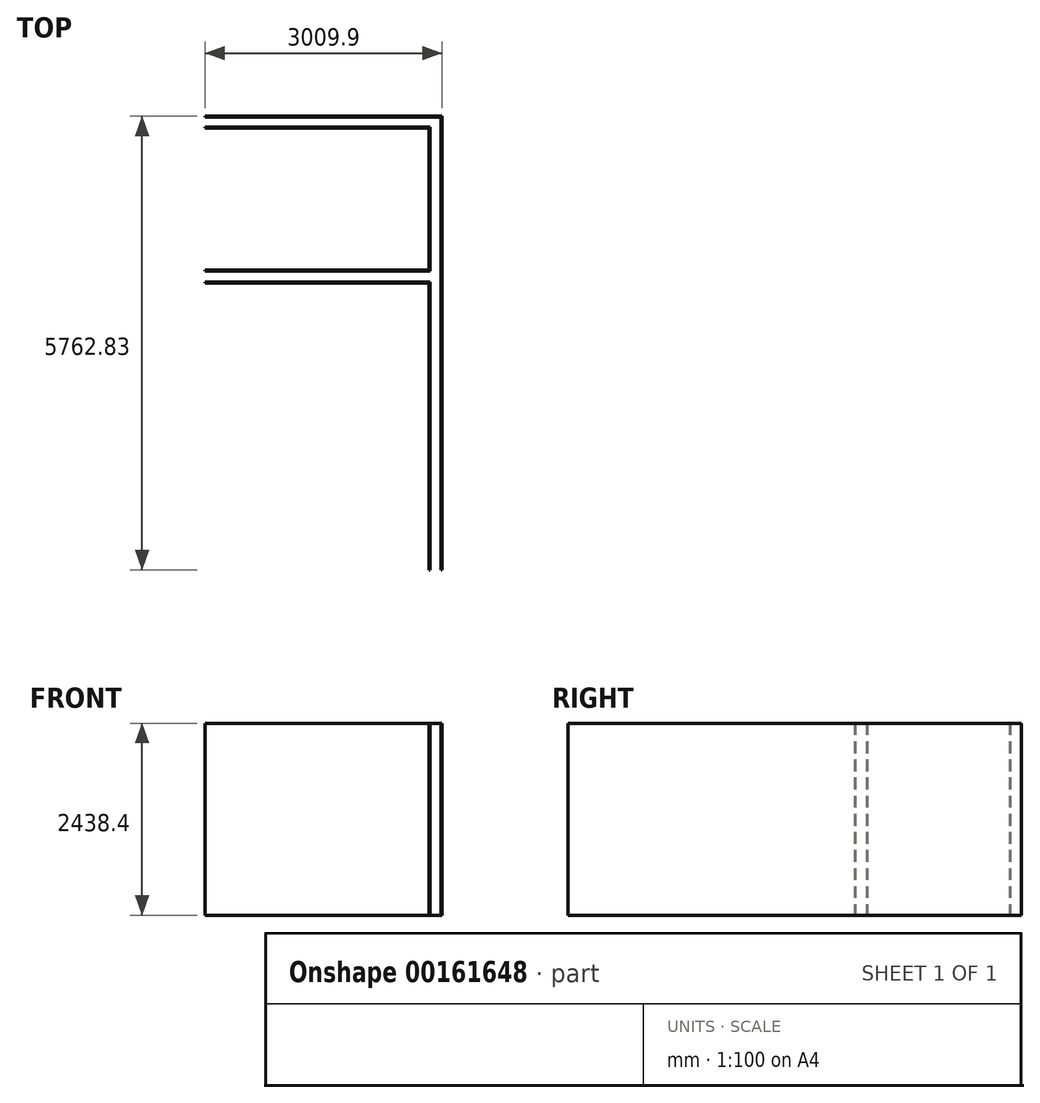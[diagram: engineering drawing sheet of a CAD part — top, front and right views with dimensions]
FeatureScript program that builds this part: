
annotation { "Feature Type Name" : "Feature", "Feature Type Description" : "" }
export const myFeature = defineFeature(function(context is Context, id is Id, definition is map)
    precondition{}
    {
        {
            var Q0;
            Q0=qCreatedBy(makeId("Top.planeOp"),FACE);
            var sketch = newSketch(context, id + "F0", { "sketchPlane" : qUnion([Q0])});
            skLineSegment(sketch, "E0", {"start": v(-8280.4, 16078.2) * mm, "end": v(-2286, 16078.2) * mm});
            skLineSegment(sketch, "E1", {"start": v(-2286, 16078.2) * mm, "end": v(-2286, 7162.8) * mm});
            skLineSegment(sketch, "E2", {"start": v(-2286, 7162.8) * mm, "end": v(0, 7162.8) * mm});
            skLineSegment(sketch, "E3", {"start": v(0, 7162.8) * mm, "end": v(0, 0) * mm});
            skLineSegment(sketch, "E4", {"start": v(0, 0) * mm, "end": v(-5283.2, 0) * mm});
            skLineSegment(sketch, "E5", {"start": v(-5283.2, 0) * mm, "end": v(-5283.2, 2286) * mm});
            skLineSegment(sketch, "E6", {"start": v(-5283.2, 2286) * mm, "end": v(-8280.4, 2286) * mm});
            skLineSegment(sketch, "E7", {"start": v(-8280.4, 2286) * mm, "end": v(-8280.4, 8201.03) * mm});
            skLineSegment(sketch, "E8", {"start": v(-8280.4, 8201.03) * mm, "end": v(-9406.5, 8900.32) * mm});
            skLineSegment(sketch, "E9", {"start": v(-9406.5, 8900.32) * mm, "end": v(-9406.5, 13223.08) * mm});
            skLineSegment(sketch, "E10", {"start": v(-9406.5, 13223.08) * mm, "end": v(-8280.4, 13922.38) * mm});
            skLineSegment(sketch, "E11", {"start": v(-8280.4, 13922.38) * mm, "end": v(-8280.4, 16078.2) * mm});
            skSolve(sketch);
        }
        {
            var Q0;
            Q0=qSketchRegion(id+"F0",true);
            extrude(context, id + "F1", {"entities" : qUnion([Q0]), "depth" : 2578.1 * mm});
        }
        {
            var Q0;
            Q0=makeQuery(id+"F1.opExtrude","CAP_FACE",FACE,{"disambiguationData":[OSD([sQuery(id+"F0.wireOp",EDGE,"E0"),sQuery(id+"F0.wireOp",EDGE,"E1"),sQuery(id+"F0.wireOp",EDGE,"E2"),sQuery(id+"F0.wireOp",EDGE,"E3"),sQuery(id+"F0.wireOp",EDGE,"E4"),sQuery(id+"F0.wireOp",EDGE,"E5"),sQuery(id+"F0.wireOp",EDGE,"E6"),sQuery(id+"F0.wireOp",EDGE,"E7"),sQuery(id+"F0.wireOp",EDGE,"E8"),sQuery(id+"F0.wireOp",EDGE,"E9"),sQuery(id+"F0.wireOp",EDGE,"E10"),sQuery(id+"F0.wireOp",EDGE,"E11")])],"isStart":false});
            shell(context, id + "F2", {"entities" : qUnion([Q0]), "thickness" : 203.2 * mm});
        }
        {
            var Q0;
            Q0=makeQuery(id+"F2.opShell","OFFSET_FACE",FACE,{"disambiguationData":[OSD([sQuery(id+"F0.wireOp",EDGE,"E6")])]});
            var sketch = newSketch(context, id + "F3", { "sketchPlane" : qUnion([Q0])});
            skLineSegment(sketch, "E12.bottom", {"start": v(5969, 2324.1) * mm, "end": v(7188.2, 2324.1) * mm});
            skLineSegment(sketch, "E12.top", {"start": v(5969, 901.7) * mm, "end": v(7188.2, 901.7) * mm});
            skLineSegment(sketch, "E12.left", {"start": v(5969, 2324.1) * mm, "end": v(5969, 901.7) * mm});
            skLineSegment(sketch, "E12.right", {"start": v(7188.2, 2324.1) * mm, "end": v(7188.2, 901.7) * mm});
            skPoint(sketch, "E13", {"position": v(6578.6, 2324.1) * mm});
            skSolve(sketch);
        }
        {
            var Q0;
            Q0=makeQuery(id+"F2.opShell","OFFSET_FACE",FACE,{"disambiguationData":[OSD([sQuery(id+"F0.wireOp",EDGE,"E0"),sQuery(id+"F0.wireOp",EDGE,"E1"),sQuery(id+"F0.wireOp",EDGE,"E2"),sQuery(id+"F0.wireOp",EDGE,"E3"),sQuery(id+"F0.wireOp",EDGE,"E4"),sQuery(id+"F0.wireOp",EDGE,"E5"),sQuery(id+"F0.wireOp",EDGE,"E6"),sQuery(id+"F0.wireOp",EDGE,"E7"),sQuery(id+"F0.wireOp",EDGE,"E8"),sQuery(id+"F0.wireOp",EDGE,"E9"),sQuery(id+"F0.wireOp",EDGE,"E10"),sQuery(id+"F0.wireOp",EDGE,"E11")])]});
            var sketch = newSketch(context, id + "F4", { "sketchPlane" : qUnion([Q0])});
            skLineSegment(sketch, "E14.bottom", {"start": v(-8077.2, 13811.9) * mm, "end": v(-7937.5, 13811.9) * mm});
            skLineSegment(sketch, "E14.top", {"start": v(-8077.2, 13850) * mm, "end": v(-7937.5, 13850) * mm});
            skLineSegment(sketch, "E14.left", {"start": v(-8077.2, 13811.9) * mm, "end": v(-8077.2, 13850) * mm});
            skLineSegment(sketch, "E14.right", {"start": v(-7937.5, 13811.9) * mm, "end": v(-7937.5, 13850) * mm});
            skLineSegment(sketch, "E15.bottom", {"start": v(-7934.96, 15875) * mm, "end": v(-7896.86, 15875) * mm});
            skLineSegment(sketch, "E15.top", {"start": v(-7934.96, 15735.3) * mm, "end": v(-7896.86, 15735.3) * mm});
            skLineSegment(sketch, "E15.left", {"start": v(-7934.96, 15875) * mm, "end": v(-7934.96, 15735.3) * mm});
            skLineSegment(sketch, "E15.right", {"start": v(-7896.86, 15875) * mm, "end": v(-7896.86, 15735.3) * mm});
            skLineSegment(sketch, "E16.bottom", {"start": v(-8077.2, 15694.66) * mm, "end": v(-7937.5, 15694.66) * mm});
            skLineSegment(sketch, "E16.top", {"start": v(-8077.2, 15732.76) * mm, "end": v(-7937.5, 15732.76) * mm});
            skLineSegment(sketch, "E16.left", {"start": v(-8077.2, 15694.66) * mm, "end": v(-8077.2, 15732.76) * mm});
            skLineSegment(sketch, "E16.right", {"start": v(-7937.5, 15694.66) * mm, "end": v(-7937.5, 15732.76) * mm});
            skLineSegment(sketch, "E17.bottom", {"start": v(-2631.44, 15875) * mm, "end": v(-2669.54, 15875) * mm});
            skLineSegment(sketch, "E17.top", {"start": v(-2631.44, 15735.3) * mm, "end": v(-2669.54, 15735.3) * mm});
            skLineSegment(sketch, "E17.left", {"start": v(-2631.44, 15875) * mm, "end": v(-2631.44, 15735.3) * mm});
            skLineSegment(sketch, "E17.right", {"start": v(-2669.54, 15875) * mm, "end": v(-2669.54, 15735.3) * mm});
            skLineSegment(sketch, "E18.bottom", {"start": v(-2489.2, 15694.66) * mm, "end": v(-2628.9, 15694.66) * mm});
            skLineSegment(sketch, "E18.top", {"start": v(-2489.2, 15732.76) * mm, "end": v(-2628.9, 15732.76) * mm});
            skLineSegment(sketch, "E18.left", {"start": v(-2489.2, 15694.66) * mm, "end": v(-2489.2, 15732.76) * mm});
            skLineSegment(sketch, "E18.right", {"start": v(-2628.9, 15694.66) * mm, "end": v(-2628.9, 15732.76) * mm});
            skLineSegment(sketch, "E19", {"start": v(-8078.22, 13808.73) * mm, "end": v(-8110.59, 13788.64) * mm});
            skLineSegment(sketch, "E20", {"start": v(-8110.59, 13788.64) * mm, "end": v(-8036.89, 13669.96) * mm});
            skLineSegment(sketch, "E21", {"start": v(-8036.89, 13669.96) * mm, "end": v(-8004.52, 13690.06) * mm});
            skLineSegment(sketch, "E22", {"start": v(-8004.52, 13690.06) * mm, "end": v(-8078.22, 13808.73) * mm});
            skLineSegment(sketch, "E23.bottom", {"start": v(-9203.3, 12669.47) * mm, "end": v(-9063.6, 12669.47) * mm});
            skLineSegment(sketch, "E23.top", {"start": v(-9203.3, 12631.37) * mm, "end": v(-9063.6, 12631.37) * mm});
            skLineSegment(sketch, "E23.left", {"start": v(-9203.3, 12669.47) * mm, "end": v(-9203.3, 12631.37) * mm});
            skLineSegment(sketch, "E23.right", {"start": v(-9063.6, 12669.47) * mm, "end": v(-9063.6, 12631.37) * mm});
            skLineSegment(sketch, "E24", {"start": v(-9162.3, 13135.53) * mm, "end": v(-9129.94, 13155.63) * mm});
            skLineSegment(sketch, "E25", {"start": v(-9129.94, 13155.63) * mm, "end": v(-9056.24, 13036.95) * mm});
            skLineSegment(sketch, "E26", {"start": v(-9056.24, 13036.95) * mm, "end": v(-9088.6, 13016.85) * mm});
            skLineSegment(sketch, "E27", {"start": v(-9088.6, 13016.85) * mm, "end": v(-9162.3, 13135.53) * mm});
            skLineSegment(sketch, "E28", {"start": v(-9162.3, 8987.87) * mm, "end": v(-9088.6, 9106.55) * mm});
            skLineSegment(sketch, "E29", {"start": v(-9088.6, 9106.55) * mm, "end": v(-9056.24, 9086.45) * mm});
            skLineSegment(sketch, "E30", {"start": v(-9056.24, 9086.45) * mm, "end": v(-9129.94, 8967.77) * mm});
            skLineSegment(sketch, "E31", {"start": v(-9129.94, 8967.77) * mm, "end": v(-9162.3, 8987.87) * mm});
            skLineSegment(sketch, "E32", {"start": v(-8109.57, 8334.13) * mm, "end": v(-8077.2, 8314.03) * mm});
            skLineSegment(sketch, "E33", {"start": v(-8077.2, 8314.03) * mm, "end": v(-8003.5, 8432.71) * mm});
            skLineSegment(sketch, "E34", {"start": v(-8003.5, 8432.71) * mm, "end": v(-8035.87, 8452.81) * mm});
            skLineSegment(sketch, "E35", {"start": v(-8035.87, 8452.81) * mm, "end": v(-8109.57, 8334.13) * mm});
            skLineSegment(sketch, "E36.bottom", {"start": v(-9203.3, 9061.59) * mm, "end": v(-9063.6, 9061.59) * mm});
            skLineSegment(sketch, "E36.top", {"start": v(-9203.3, 9099.69) * mm, "end": v(-9063.6, 9099.69) * mm});
            skLineSegment(sketch, "E36.left", {"start": v(-9203.3, 9061.59) * mm, "end": v(-9203.3, 9099.69) * mm});
            skLineSegment(sketch, "E36.right", {"start": v(-9063.6, 9061.59) * mm, "end": v(-9063.6, 9099.69) * mm});
            skLineSegment(sketch, "E37.bottom", {"start": v(-8077.2, 8311.5) * mm, "end": v(-7937.5, 8311.5) * mm});
            skLineSegment(sketch, "E37.top", {"start": v(-8077.2, 8273.4) * mm, "end": v(-7937.5, 8273.4) * mm});
            skLineSegment(sketch, "E37.left", {"start": v(-8077.2, 8311.5) * mm, "end": v(-8077.2, 8273.4) * mm});
            skLineSegment(sketch, "E37.right", {"start": v(-7937.5, 8311.5) * mm, "end": v(-7937.5, 8273.4) * mm});
            skLineSegment(sketch, "E38.bottom", {"start": v(-8077.2, 2631.44) * mm, "end": v(-7937.5, 2631.44) * mm});
            skLineSegment(sketch, "E38.top", {"start": v(-8077.2, 2669.54) * mm, "end": v(-7937.5, 2669.54) * mm});
            skLineSegment(sketch, "E38.left", {"start": v(-8077.2, 2631.44) * mm, "end": v(-8077.2, 2669.54) * mm});
            skLineSegment(sketch, "E38.right", {"start": v(-7937.5, 2631.44) * mm, "end": v(-7937.5, 2669.54) * mm});
            skLineSegment(sketch, "E39.bottom", {"start": v(-7896.86, 2489.2) * mm, "end": v(-7934.96, 2489.2) * mm});
            skLineSegment(sketch, "E39.top", {"start": v(-7896.86, 2628.9) * mm, "end": v(-7934.96, 2628.9) * mm});
            skLineSegment(sketch, "E39.left", {"start": v(-7896.86, 2489.2) * mm, "end": v(-7896.86, 2628.9) * mm});
            skLineSegment(sketch, "E39.right", {"start": v(-7934.96, 2489.2) * mm, "end": v(-7934.96, 2628.9) * mm});
            skLineSegment(sketch, "E40.bottom", {"start": v(-5082.54, 2489.2) * mm, "end": v(-5120.64, 2489.2) * mm});
            skLineSegment(sketch, "E40.top", {"start": v(-5082.54, 2628.9) * mm, "end": v(-5120.64, 2628.9) * mm});
            skLineSegment(sketch, "E40.left", {"start": v(-5082.54, 2489.2) * mm, "end": v(-5082.54, 2628.9) * mm});
            skLineSegment(sketch, "E40.right", {"start": v(-5120.64, 2489.2) * mm, "end": v(-5120.64, 2628.9) * mm});
            skLineSegment(sketch, "E41.top", {"start": v(-5080, 2448.56) * mm, "end": v(-4940.3, 2448.56) * mm});
            skLineSegment(sketch, "E41.right", {"start": v(-4940.3, 2486.66) * mm, "end": v(-4940.3, 2448.56) * mm});
            skLineSegment(sketch, "E42.bottom", {"start": v(-5080, 345.44) * mm, "end": v(-4940.3, 345.44) * mm});
            skLineSegment(sketch, "E42.top", {"start": v(-5080, 383.54) * mm, "end": v(-4940.3, 383.54) * mm});
            skLineSegment(sketch, "E42.left", {"start": v(-5080, 345.44) * mm, "end": v(-5080, 383.54) * mm});
            skLineSegment(sketch, "E42.right", {"start": v(-4940.3, 345.44) * mm, "end": v(-4940.3, 383.54) * mm});
            skLineSegment(sketch, "E43.bottom", {"start": v(-4937.76, 203.2) * mm, "end": v(-4899.66, 203.2) * mm});
            skLineSegment(sketch, "E43.top", {"start": v(-4937.76, 342.9) * mm, "end": v(-4899.66, 342.9) * mm});
            skLineSegment(sketch, "E43.left", {"start": v(-4937.76, 203.2) * mm, "end": v(-4937.76, 342.9) * mm});
            skLineSegment(sketch, "E43.right", {"start": v(-4899.66, 203.2) * mm, "end": v(-4899.66, 342.9) * mm});
            skLineSegment(sketch, "E44.bottom", {"start": v(-383.54, 203.2) * mm, "end": v(-345.44, 203.2) * mm});
            skLineSegment(sketch, "E44.top", {"start": v(-383.54, 342.9) * mm, "end": v(-345.44, 342.9) * mm});
            skLineSegment(sketch, "E44.left", {"start": v(-383.54, 203.2) * mm, "end": v(-383.54, 342.9) * mm});
            skLineSegment(sketch, "E44.right", {"start": v(-345.44, 203.2) * mm, "end": v(-345.44, 342.9) * mm});
            skLineSegment(sketch, "E45.bottom", {"start": v(-203.2, 345.44) * mm, "end": v(-342.9, 345.44) * mm});
            skLineSegment(sketch, "E45.top", {"start": v(-203.2, 383.54) * mm, "end": v(-342.9, 383.54) * mm});
            skLineSegment(sketch, "E45.left", {"start": v(-203.2, 345.44) * mm, "end": v(-203.2, 383.54) * mm});
            skLineSegment(sketch, "E45.right", {"start": v(-342.9, 345.44) * mm, "end": v(-342.9, 383.54) * mm});
            skLineSegment(sketch, "E46.bottom", {"start": v(-203.2, 6779.26) * mm, "end": v(-342.9, 6779.26) * mm});
            skLineSegment(sketch, "E46.top", {"start": v(-203.2, 6817.36) * mm, "end": v(-342.9, 6817.36) * mm});
            skLineSegment(sketch, "E46.left", {"start": v(-203.2, 6779.26) * mm, "end": v(-203.2, 6817.36) * mm});
            skLineSegment(sketch, "E46.right", {"start": v(-342.9, 6779.26) * mm, "end": v(-342.9, 6817.36) * mm});
            skLineSegment(sketch, "E47.bottom", {"start": v(-345.44, 6959.6) * mm, "end": v(-383.54, 6959.6) * mm});
            skLineSegment(sketch, "E47.top", {"start": v(-345.44, 6819.9) * mm, "end": v(-383.54, 6819.9) * mm});
            skLineSegment(sketch, "E47.left", {"start": v(-345.44, 6959.6) * mm, "end": v(-345.44, 6819.9) * mm});
            skLineSegment(sketch, "E47.right", {"start": v(-383.54, 6959.6) * mm, "end": v(-383.54, 6819.9) * mm});
            skLineSegment(sketch, "E48", {"start": v(-4940.3, 2486.66) * mm, "end": v(-5080, 2486.66) * mm});
            skLineSegment(sketch, "E49", {"start": v(-5080, 2486.66) * mm, "end": v(-5080, 2448.56) * mm});
            skLineSegment(sketch, "E50", {"start": v(-9203.3, 13110.07) * mm, "end": v(-9045.7, 12987.43) * mm, "construction": true});
            skLineSegment(sketch, "E51", {"start": v(-9045.7, 12987.43) * mm, "end": v(-9104.83, 13171.22) * mm, "construction": true});
            skLineSegment(sketch, "E52", {"start": v(-9104.83, 13171.22) * mm, "end": v(-9203.3, 12968.55) * mm, "construction": true});
            skLineSegment(sketch, "E53", {"start": v(-9203.3, 12968.55) * mm, "end": v(-9045.7, 12987.43) * mm, "construction": true});
            skSolve(sketch);
        }
        {
            var Q0;
            Q0=qSketchRegion(id+"F3",true);
            var Q1;
            Q1=makeQuery(id+"FwcOo8eikqoZCvb_1.opExtrude","SWEPT_FACE",FACE,{"disambiguationData":[OSD([sQuery(id+"F7.wireOp",EDGE,"E55.top"),sQuery(id+"F7.wireOp",EDGE,"E63")])]});
            extrude(context, id + "F5", {"entities" : qUnion([Q0]), "operationType" : NewBodyOperationType.REMOVE, "endBound" : BoundingType.UP_TO_NEXT, "oppositeDirection" : true, "depth" : 25.4 * mm});
        }
        {
            var Q0;
            Q0=qSketchRegion(id+"F4",true);
            extrude(context, id + "F6", {"entities" : qUnion([Q0]), "operationType" : NewBodyOperationType.ADD, "depth" : 2349.5 * mm});
        }
        {
            var Q0;
            Q0=makeQuery(id+"F2.opShell","OFFSET_FACE",FACE,{"disambiguationData":[OSD([sQuery(id+"F0.wireOp",EDGE,"E0"),sQuery(id+"F0.wireOp",EDGE,"E1"),sQuery(id+"F0.wireOp",EDGE,"E2"),sQuery(id+"F0.wireOp",EDGE,"E3"),sQuery(id+"F0.wireOp",EDGE,"E4"),sQuery(id+"F0.wireOp",EDGE,"E5"),sQuery(id+"F0.wireOp",EDGE,"E6"),sQuery(id+"F0.wireOp",EDGE,"E7"),sQuery(id+"F0.wireOp",EDGE,"E8"),sQuery(id+"F0.wireOp",EDGE,"E9"),sQuery(id+"F0.wireOp",EDGE,"E10"),sQuery(id+"F0.wireOp",EDGE,"E11")])]});
            var sketch = newSketch(context, id + "F7", { "sketchPlane" : qUnion([Q0])});
            skLineSegment(sketch, "E54.bottom", {"start": v(-7937.5, 8391.73) * mm, "end": v(-7924.8, 8391.73) * mm, "construction": true});
            skLineSegment(sketch, "E54.top", {"start": v(-7937.5, 2641.6) * mm, "end": v(-7924.8, 2641.6) * mm, "construction": true});
            skLineSegment(sketch, "E54.left", {"start": v(-7937.5, 8391.73) * mm, "end": v(-7937.5, 2641.6) * mm});
            skLineSegment(sketch, "E54.right", {"start": v(-7924.8, 8391.73) * mm, "end": v(-7924.8, 2641.6) * mm});
            skLineSegment(sketch, "E55.bottom", {"start": v(-7924.8, 2628.9) * mm, "end": v(-4940.3, 2628.9) * mm});
            skLineSegment(sketch, "E55.top", {"start": v(-7924.8, 2641.6) * mm, "end": v(-4940.3, 2641.6) * mm});
            skLineSegment(sketch, "E55.left", {"start": v(-7924.8, 2628.9) * mm, "end": v(-7924.8, 2641.6) * mm, "construction": true});
            skLineSegment(sketch, "E55.right", {"start": v(-4940.3, 2628.9) * mm, "end": v(-4940.3, 2641.6) * mm, "construction": true});
            skLineSegment(sketch, "E56", {"start": v(-7924.8, 2628.9) * mm, "end": v(-7937.5, 2628.9) * mm});
            skLineSegment(sketch, "E57", {"start": v(-7937.5, 2628.9) * mm, "end": v(-7937.5, 2641.6) * mm});
            skLineSegment(sketch, "E58.bottom", {"start": v(-4940.3, 2628.9) * mm, "end": v(-4927.6, 2628.9) * mm, "construction": true});
            skLineSegment(sketch, "E58.top", {"start": v(-4940.3, 355.6) * mm, "end": v(-4927.6, 355.6) * mm, "construction": true});
            skLineSegment(sketch, "E58.left", {"start": v(-4940.3, 2628.9) * mm, "end": v(-4940.3, 355.6) * mm});
            skLineSegment(sketch, "E58.right", {"start": v(-4927.6, 2628.9) * mm, "end": v(-4927.6, 355.6) * mm});
            skLineSegment(sketch, "E59.bottom", {"start": v(-4927.6, 342.9) * mm, "end": v(-355.6, 342.9) * mm});
            skLineSegment(sketch, "E59.top", {"start": v(-4927.6, 355.6) * mm, "end": v(-355.6, 355.6) * mm});
            skLineSegment(sketch, "E59.left", {"start": v(-4927.6, 342.9) * mm, "end": v(-4927.6, 355.6) * mm, "construction": true});
            skLineSegment(sketch, "E59.right", {"start": v(-355.6, 342.9) * mm, "end": v(-355.6, 355.6) * mm, "construction": true});
            skLineSegment(sketch, "E60", {"start": v(-4940.3, 355.6) * mm, "end": v(-4940.3, 342.9) * mm});
            skLineSegment(sketch, "E61", {"start": v(-4940.3, 342.9) * mm, "end": v(-4927.6, 342.9) * mm});
            skLineSegment(sketch, "E62", {"start": v(-4927.6, 2628.9) * mm, "end": v(-4927.6, 2641.6) * mm});
            skLineSegment(sketch, "E63", {"start": v(-4940.3, 2641.6) * mm, "end": v(-4927.6, 2641.6) * mm});
            skLineSegment(sketch, "E64.bottom", {"start": v(-355.6, 355.6) * mm, "end": v(-342.9, 355.6) * mm, "construction": true});
            skLineSegment(sketch, "E64.top", {"start": v(-355.6, 6019.58) * mm, "end": v(-342.9, 6019.58) * mm});
            skLineSegment(sketch, "E64.left", {"start": v(-355.6, 355.6) * mm, "end": v(-355.6, 6019.58) * mm});
            skLineSegment(sketch, "E64.right", {"start": v(-342.9, 355.6) * mm, "end": v(-342.9, 6019.58) * mm});
            skLineSegment(sketch, "E65", {"start": v(-355.6, 342.9) * mm, "end": v(-342.9, 342.9) * mm});
            skLineSegment(sketch, "E66", {"start": v(-342.9, 342.9) * mm, "end": v(-342.9, 355.6) * mm});
            skLineSegment(sketch, "E67", {"start": v(-7937.5, 8391.73) * mm, "end": v(-9063.6, 9091.02) * mm});
            skLineSegment(sketch, "E68", {"start": v(-9063.6, 9091.02) * mm, "end": v(-9063.6, 13032.38) * mm});
            skLineSegment(sketch, "E69", {"start": v(-9063.6, 13032.38) * mm, "end": v(-7937.5, 13731.67) * mm});
            skLineSegment(sketch, "E70", {"start": v(-7937.5, 13731.67) * mm, "end": v(-7937.5, 15735.3) * mm});
            skLineSegment(sketch, "E71", {"start": v(-7937.5, 15735.3) * mm, "end": v(-2628.9, 15735.3) * mm});
            skLineSegment(sketch, "E72", {"start": v(-2628.9, 15735.3) * mm, "end": v(-2628.9, 11339.58) * mm});
            skLineSegment(sketch, "E73", {"start": v(-2628.9, 11339.58) * mm, "end": v(-2641.6, 11339.58) * mm});
            skLineSegment(sketch, "E74", {"start": v(-2641.6, 11339.58) * mm, "end": v(-2641.6, 15722.6) * mm});
            skLineSegment(sketch, "E75", {"start": v(-2641.6, 15722.6) * mm, "end": v(-7924.8, 15722.6) * mm});
            skLineSegment(sketch, "E76", {"start": v(-7924.8, 15722.6) * mm, "end": v(-7924.8, 13724.61) * mm});
            skLineSegment(sketch, "E77", {"start": v(-7924.8, 13724.61) * mm, "end": v(-9050.9, 13025.32) * mm});
            skLineSegment(sketch, "E78", {"start": v(-9050.9, 13025.32) * mm, "end": v(-9050.9, 9098.08) * mm});
            skLineSegment(sketch, "E79", {"start": v(-9050.9, 9098.08) * mm, "end": v(-7924.8, 8398.79) * mm});
            skLineSegment(sketch, "E80", {"start": v(-8493.85, 8752.16) * mm, "end": v(-8500.55, 8741.37) * mm, "construction": true});
            skLineSegment(sketch, "E81", {"start": v(-9063.6, 11061.7) * mm, "end": v(-9050.9, 11061.7) * mm, "construction": true});
            skLineSegment(sketch, "E82", {"start": v(-8487.85, 13374.97) * mm, "end": v(-8494.55, 13385.75) * mm, "construction": true});
            skLineSegment(sketch, "E83", {"start": v(-7924.8, 15722.6) * mm, "end": v(-7937.5, 15722.6) * mm, "construction": true});
            skLineSegment(sketch, "E84", {"start": v(-2641.6, 15735.3) * mm, "end": v(-2641.6, 15722.6) * mm, "construction": true});
            skLineSegment(sketch, "E85", {"start": v(-7924.8, 8391.73) * mm, "end": v(-7924.8, 8398.79) * mm});
            skSolve(sketch);
        }
        {
            var Q0;
            Q0=qSketchRegion(id+"F7",true);
            extrude(context, id + "F8", {"entities" : qUnion([Q0]), "depth" : 12 * 203.2 * mm});
        }
        {
            var Q0;
            Q0=qSketchRegion(id+"F3",true);
            var Q1;
            Q1=makeQuery(id+"F8.opExtrude","SWEPT_FACE",FACE,{"disambiguationData":[OSD([sQuery(id+"F7.wireOp",EDGE,"E55.top"),sQuery(id+"F7.wireOp",EDGE,"E63")])]});
            extrude(context, id + "F9", {"entities" : qUnion([Q0]), "operationType" : NewBodyOperationType.REMOVE, "endBound" : BoundingType.UP_TO_SURFACE, "endBoundEntityFace" : qUnion([Q1]), "depth" : 25.4 * mm});
        }
        {
            var Q0;
            Q0=qCreatedBy(makeId("Top.planeOp"),FACE);
            var sketch = newSketch(context, id + "F10", { "sketchPlane" : qUnion([Q0])});
            skLineSegment(sketch, "E86", {"start": v(-8077.2, 2489.2) * mm, "end": v(-8077.2, 8314.03) * mm});
            skLineSegment(sketch, "E87", {"start": v(-8077.2, 8314.03) * mm, "end": v(-9203.3, 9013.33) * mm});
            skLineSegment(sketch, "E88", {"start": v(-9203.3, 9013.33) * mm, "end": v(-9203.3, 13110.07) * mm});
            skLineSegment(sketch, "E89", {"start": v(-9203.3, 13110.07) * mm, "end": v(-8077.2, 13809.37) * mm});
            skLineSegment(sketch, "E90", {"start": v(-8077.2, 13809.37) * mm, "end": v(-8077.2, 15875) * mm});
            skLineSegment(sketch, "E91", {"start": v(-8077.2, 15875) * mm, "end": v(-2489.2, 15875) * mm});
            skLineSegment(sketch, "E92", {"start": v(-2489.2, 15875) * mm, "end": v(-2489.2, 11339.58) * mm});
            skLineSegment(sketch, "E93", {"start": v(-2489.2, 11339.58) * mm, "end": v(-2628.9, 11339.58) * mm});
            skLineSegment(sketch, "E94", {"start": v(-2628.9, 11339.58) * mm, "end": v(-2628.9, 15735.3) * mm});
            skLineSegment(sketch, "E95", {"start": v(-7937.5, 15735.3) * mm, "end": v(-7937.5, 13731.67) * mm});
            skLineSegment(sketch, "E96", {"start": v(-7937.5, 13731.67) * mm, "end": v(-9063.6, 13032.38) * mm});
            skLineSegment(sketch, "E97", {"start": v(-9063.6, 13032.38) * mm, "end": v(-9063.6, 9091.02) * mm});
            skLineSegment(sketch, "E98", {"start": v(-9063.6, 9091.02) * mm, "end": v(-7937.5, 8391.73) * mm});
            skLineSegment(sketch, "E99", {"start": v(-7937.5, 8391.73) * mm, "end": v(-7937.5, 2628.9) * mm});
            skLineSegment(sketch, "E100", {"start": v(-7937.5, 2628.9) * mm, "end": v(-4940.3, 2628.9) * mm});
            skLineSegment(sketch, "E101", {"start": v(-4940.3, 2628.9) * mm, "end": v(-4940.3, 342.9) * mm});
            skLineSegment(sketch, "E102", {"start": v(-4940.3, 342.9) * mm, "end": v(-342.9, 342.9) * mm});
            skLineSegment(sketch, "E103", {"start": v(-342.9, 342.9) * mm, "end": v(-342.9, 5526.42) * mm});
            skLineSegment(sketch, "E104", {"start": v(-342.9, 5526.42) * mm, "end": v(-203.2, 5526.42) * mm});
            skLineSegment(sketch, "E105", {"start": v(-203.2, 5526.42) * mm, "end": v(-203.2, 203.2) * mm});
            skLineSegment(sketch, "E106", {"start": v(-203.2, 203.2) * mm, "end": v(-5080, 203.2) * mm});
            skLineSegment(sketch, "E107", {"start": v(-5080, 203.2) * mm, "end": v(-5080, 2489.2) * mm});
            skLineSegment(sketch, "E108", {"start": v(-5080, 2489.2) * mm, "end": v(-8077.2, 2489.2) * mm});
            skLineSegment(sketch, "E109", {"start": v(-9203.3, 11061.7) * mm, "end": v(-9063.6, 11061.7) * mm, "construction": true});
            skLineSegment(sketch, "E110", {"start": v(-8566.55, 13341.04) * mm, "end": v(-8640.25, 13459.72) * mm, "construction": true});
            skLineSegment(sketch, "E111", {"start": v(-8077.2, 14842.18) * mm, "end": v(-7937.5, 14842.18) * mm, "construction": true});
            skLineSegment(sketch, "E112", {"start": v(-2489.2, 13607.29) * mm, "end": v(-2628.9, 13607.29) * mm, "construction": true});
            skLineSegment(sketch, "E113", {"start": v(-7937.5, 15735.3) * mm, "end": v(-2628.9, 15735.3) * mm});
            skLineSegment(sketch, "E114", {"start": v(-5283.2, 15735.3) * mm, "end": v(-5283.2, 15875) * mm, "construction": true});
            skLineSegment(sketch, "E115", {"start": v(-8640.25, 8663.68) * mm, "end": v(-8566.55, 8782.36) * mm, "construction": true});
            skLineSegment(sketch, "E116", {"start": v(-7937.5, 5401.62) * mm, "end": v(-8077.2, 5401.62) * mm, "construction": true});
            skLineSegment(sketch, "E117", {"start": v(-6578.6, 2489.2) * mm, "end": v(-6578.6, 2628.9) * mm, "construction": true});
            skSolve(sketch);
        }
        {
            var Q0;
            Q0 = qSketchRegion(id + "F10", true);
            extrude(context, id + "F11", {"entities" : qUnion([Q0]), "depth" : 12.7 * mm});
        }
        {
            var Q0;
            Q0=qCreatedBy(makeId("Top.planeOp"),FACE);
            var sketch = newSketch(context, id + "F12", { "sketchPlane" : qUnion([Q0])});
            skLineSegment(sketch, "E118.bottom", {"start": v(-4940.3, 2628.9) * mm, "end": v(-5080, 2628.9) * mm});
            skLineSegment(sketch, "E118.top", {"start": v(-4940.3, 8252.03) * mm, "end": v(-5080, 8252.03) * mm, "construction": true});
            skLineSegment(sketch, "E118.left", {"start": v(-4940.3, 2628.9) * mm, "end": v(-4940.3, 8252.03) * mm});
            skLineSegment(sketch, "E118.right", {"start": v(-5080, 2628.9) * mm, "end": v(-5080, 8252.03) * mm});
            skLineSegment(sketch, "E119.bottom", {"start": v(-5082.54, 6423.23) * mm, "end": v(-7937.5, 6423.23) * mm});
            skLineSegment(sketch, "E119.top", {"start": v(-5082.54, 6283.53) * mm, "end": v(-7937.5, 6283.53) * mm});
            skLineSegment(sketch, "E119.left", {"start": v(-5082.54, 6423.23) * mm, "end": v(-5082.54, 6283.53) * mm});
            skLineSegment(sketch, "E119.right", {"start": v(-7937.5, 6423.23) * mm, "end": v(-7937.5, 6283.53) * mm});
            skLineSegment(sketch, "E120.bottom", {"start": v(-5080, 8252.03) * mm, "end": v(-7937.5, 8252.03) * mm});
            skLineSegment(sketch, "E120.top", {"start": v(-5080, 8391.73) * mm, "end": v(-7937.5, 8391.73) * mm});
            skLineSegment(sketch, "E120.left", {"start": v(-5080, 8252.03) * mm, "end": v(-5080, 8391.73) * mm, "construction": true});
            skLineSegment(sketch, "E120.right", {"start": v(-7937.5, 8252.03) * mm, "end": v(-7937.5, 8391.73) * mm});
            skLineSegment(sketch, "E121", {"start": v(-5080, 8391.73) * mm, "end": v(-4940.3, 8391.73) * mm});
            skLineSegment(sketch, "E122", {"start": v(-4940.3, 8391.73) * mm, "end": v(-4940.3, 8252.03) * mm});
            skSolve(sketch);
        }
        {
            var Q0;
            Q0=qCreatedBy(makeId("Top.planeOp"),FACE);
            var sketch = newSketch(context, id + "F13", { "sketchPlane" : qUnion([Q0])});
            skLineSegment(sketch, "E123.bottom", {"start": v(-5080, 2628.9) * mm, "end": v(-5092.7, 2628.9) * mm});
            skLineSegment(sketch, "E123.top", {"start": v(-5080, 6270.83) * mm, "end": v(-5092.7, 6270.83) * mm, "construction": true});
            skLineSegment(sketch, "E123.left", {"start": v(-5080, 2628.9) * mm, "end": v(-5080, 6270.83) * mm});
            skLineSegment(sketch, "E123.right", {"start": v(-5092.7, 2628.9) * mm, "end": v(-5092.7, 6270.83) * mm});
            skLineSegment(sketch, "E124.bottom", {"start": v(-5092.7, 6270.83) * mm, "end": v(-7937.5, 6270.83) * mm});
            skLineSegment(sketch, "E124.top", {"start": v(-5092.7, 6283.53) * mm, "end": v(-7937.5, 6283.53) * mm});
            skLineSegment(sketch, "E124.left", {"start": v(-5092.7, 6270.83) * mm, "end": v(-5092.7, 6283.53) * mm, "construction": true});
            skLineSegment(sketch, "E124.right", {"start": v(-7937.5, 6270.83) * mm, "end": v(-7937.5, 6283.53) * mm});
            skLineSegment(sketch, "E125.bottom", {"start": v(-7937.5, 6423.23) * mm, "end": v(-5092.7, 6423.23) * mm});
            skLineSegment(sketch, "E125.top", {"start": v(-7937.5, 6435.93) * mm, "end": v(-5092.7, 6435.93) * mm});
            skLineSegment(sketch, "E125.left", {"start": v(-7937.5, 6423.23) * mm, "end": v(-7937.5, 6435.93) * mm});
            skLineSegment(sketch, "E125.right", {"start": v(-5092.7, 6423.23) * mm, "end": v(-5092.7, 6435.93) * mm, "construction": true});
            skLineSegment(sketch, "E126.bottom", {"start": v(-5092.7, 6435.93) * mm, "end": v(-5080, 6435.93) * mm, "construction": true});
            skLineSegment(sketch, "E126.top", {"start": v(-5092.7, 8239.33) * mm, "end": v(-5080, 8239.33) * mm, "construction": true});
            skLineSegment(sketch, "E126.left", {"start": v(-5092.7, 6435.93) * mm, "end": v(-5092.7, 8239.33) * mm});
            skLineSegment(sketch, "E126.right", {"start": v(-5080, 6435.93) * mm, "end": v(-5080, 8239.33) * mm});
            skLineSegment(sketch, "E127.bottom", {"start": v(-5092.7, 8239.33) * mm, "end": v(-7937.5, 8239.33) * mm});
            skLineSegment(sketch, "E127.top", {"start": v(-5092.7, 8252.03) * mm, "end": v(-7937.5, 8252.03) * mm});
            skLineSegment(sketch, "E127.left", {"start": v(-5092.7, 8239.33) * mm, "end": v(-5092.7, 8252.03) * mm, "construction": true});
            skLineSegment(sketch, "E127.right", {"start": v(-7937.5, 8239.33) * mm, "end": v(-7937.5, 8252.03) * mm});
            skLineSegment(sketch, "E128.bottom", {"start": v(-4940.3, 2628.9) * mm, "end": v(-4927.6, 2628.9) * mm});
            skLineSegment(sketch, "E128.top", {"start": v(-4940.3, 8379.03) * mm, "end": v(-4927.6, 8379.03) * mm, "construction": true});
            skLineSegment(sketch, "E128.left", {"start": v(-4940.3, 2628.9) * mm, "end": v(-4940.3, 8379.03) * mm});
            skLineSegment(sketch, "E128.right", {"start": v(-4927.6, 2628.9) * mm, "end": v(-4927.6, 8379.03) * mm});
            skLineSegment(sketch, "E129.bottom", {"start": v(-7937.5, 8379.03) * mm, "end": v(-4940.3, 8379.03) * mm});
            skLineSegment(sketch, "E129.top", {"start": v(-7937.5, 8391.73) * mm, "end": v(-4940.3, 8391.73) * mm});
            skLineSegment(sketch, "E129.left", {"start": v(-7937.5, 8379.03) * mm, "end": v(-7937.5, 8391.73) * mm});
            skLineSegment(sketch, "E129.right", {"start": v(-4940.3, 8379.03) * mm, "end": v(-4940.3, 8391.73) * mm, "construction": true});
            skLineSegment(sketch, "E130", {"start": v(-5092.7, 6283.53) * mm, "end": v(-5080, 6283.53) * mm});
            skLineSegment(sketch, "E131", {"start": v(-5080, 6283.53) * mm, "end": v(-5080, 6270.83) * mm});
            skLineSegment(sketch, "E132", {"start": v(-5092.7, 6423.23) * mm, "end": v(-5080, 6423.23) * mm});
            skLineSegment(sketch, "E133", {"start": v(-5080, 6423.23) * mm, "end": v(-5080, 6435.93) * mm});
            skLineSegment(sketch, "E134", {"start": v(-5092.7, 8252.03) * mm, "end": v(-5080, 8252.03) * mm});
            skLineSegment(sketch, "E135", {"start": v(-5080, 8252.03) * mm, "end": v(-5080, 8239.33) * mm});
            skLineSegment(sketch, "E136", {"start": v(-4940.3, 8391.73) * mm, "end": v(-4927.6, 8391.73) * mm});
            skLineSegment(sketch, "E137", {"start": v(-4927.6, 8391.73) * mm, "end": v(-4927.6, 8379.03) * mm});
            skSolve(sketch);
        }
        {
            var Q0;
            Q0 = qSketchRegion(id + "F13", true);
            extrude(context, id + "F14", {"entities" : qUnion([Q0]), "depth" : 2438.4 * mm});
        }
        {
            var Q0;
            Q0=makeQuery(id+"F1.opExtrude","SWEPT_BODY",BODY,{"disambiguationData":[OSD([sQuery(id+"F0.wireOp",EDGE,"E0"),sQuery(id+"F0.wireOp",EDGE,"E1"),sQuery(id+"F0.wireOp",EDGE,"E2"),sQuery(id+"F0.wireOp",EDGE,"E3"),sQuery(id+"F0.wireOp",EDGE,"E4"),sQuery(id+"F0.wireOp",EDGE,"E5"),sQuery(id+"F0.wireOp",EDGE,"E6"),sQuery(id+"F0.wireOp",EDGE,"E7"),sQuery(id+"F0.wireOp",EDGE,"E8"),sQuery(id+"F0.wireOp",EDGE,"E9"),sQuery(id+"F0.wireOp",EDGE,"E10"),sQuery(id+"F0.wireOp",EDGE,"E11")])]});
            deleteBodies(context, id + "F15", {"entities" : qUnion([Q0])});
        }
        {
            var Q0;
            Q0=makeQuery(id+"F8.opExtrude","SWEPT_BODY",BODY,{"disambiguationData":[OSD([sQuery(id+"F7.wireOp",EDGE,"E54.left"),sQuery(id+"F7.wireOp",EDGE,"E54.right"),sQuery(id+"F7.wireOp",EDGE,"E55.bottom"),sQuery(id+"F7.wireOp",EDGE,"E55.top"),sQuery(id+"F7.wireOp",EDGE,"E56"),sQuery(id+"F7.wireOp",EDGE,"E57"),sQuery(id+"F7.wireOp",EDGE,"E58.left"),sQuery(id+"F7.wireOp",EDGE,"E58.right"),sQuery(id+"F7.wireOp",EDGE,"E59.bottom"),sQuery(id+"F7.wireOp",EDGE,"E59.top"),sQuery(id+"F7.wireOp",EDGE,"E60"),sQuery(id+"F7.wireOp",EDGE,"E61"),sQuery(id+"F7.wireOp",EDGE,"E62"),sQuery(id+"F7.wireOp",EDGE,"E63"),sQuery(id+"F7.wireOp",EDGE,"E64.top"),sQuery(id+"F7.wireOp",EDGE,"E64.left"),sQuery(id+"F7.wireOp",EDGE,"E64.right"),sQuery(id+"F7.wireOp",EDGE,"E65"),sQuery(id+"F7.wireOp",EDGE,"E66"),sQuery(id+"F7.wireOp",EDGE,"E67"),sQuery(id+"F7.wireOp",EDGE,"E68"),sQuery(id+"F7.wireOp",EDGE,"E69"),sQuery(id+"F7.wireOp",EDGE,"E70"),sQuery(id+"F7.wireOp",EDGE,"E71"),sQuery(id+"F7.wireOp",EDGE,"E72"),sQuery(id+"F7.wireOp",EDGE,"E73"),sQuery(id+"F7.wireOp",EDGE,"E74"),sQuery(id+"F7.wireOp",EDGE,"E75"),sQuery(id+"F7.wireOp",EDGE,"E76"),sQuery(id+"F7.wireOp",EDGE,"E77"),sQuery(id+"F7.wireOp",EDGE,"E78"),sQuery(id+"F7.wireOp",EDGE,"E79"),sQuery(id+"F7.wireOp",EDGE,"E85")])]});
            deleteBodies(context, id + "F16", {"entities" : qUnion([Q0])});
        }
        {
            var Q0;
            Q0=makeQuery(id+"F11.opExtrude","SWEPT_BODY",BODY,{"disambiguationData":[OSD([sQuery(id+"F10.wireOp",EDGE,"E86"),sQuery(id+"F10.wireOp",EDGE,"E87"),sQuery(id+"F10.wireOp",EDGE,"E88"),sQuery(id+"F10.wireOp",EDGE,"E89"),sQuery(id+"F10.wireOp",EDGE,"E90"),sQuery(id+"F10.wireOp",EDGE,"E91"),sQuery(id+"F10.wireOp",EDGE,"E92"),sQuery(id+"F10.wireOp",EDGE,"E93"),sQuery(id+"F10.wireOp",EDGE,"E94"),sQuery(id+"F10.wireOp",EDGE,"E95"),sQuery(id+"F10.wireOp",EDGE,"E96"),sQuery(id+"F10.wireOp",EDGE,"E97"),sQuery(id+"F10.wireOp",EDGE,"E98"),sQuery(id+"F10.wireOp",EDGE,"E99"),sQuery(id+"F10.wireOp",EDGE,"E100"),sQuery(id+"F10.wireOp",EDGE,"E101"),sQuery(id+"F10.wireOp",EDGE,"E102"),sQuery(id+"F10.wireOp",EDGE,"E103"),sQuery(id+"F10.wireOp",EDGE,"E104"),sQuery(id+"F10.wireOp",EDGE,"E105"),sQuery(id+"F10.wireOp",EDGE,"E106"),sQuery(id+"F10.wireOp",EDGE,"E107"),sQuery(id+"F10.wireOp",EDGE,"E108"),sQuery(id+"F10.wireOp",EDGE,"E113")])]});
            deleteBodies(context, id + "F17", {"entities" : qUnion([Q0])});
        }
    });
